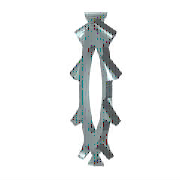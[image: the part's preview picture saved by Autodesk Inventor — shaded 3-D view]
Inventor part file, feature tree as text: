
AUTODESK INVENTOR PART (.ipt)
format: ipt  version: 2011 (Build 150229000, 229)  size: 162,304 bytes
history: native  units: mm (DEFAULTED — no unit token found)
features: extrude x1, pattern_circular x1, other x1, plane x1
ambient origin geometry x7: Origin, YZ Plane, XY Plane, X Axis, Y Axis, Z Axis, Center Point
bodies: Body (feature_tree)
feature tree (4):
  extrude  "Cut"  Depth=14.0mm
  pattern_circular  "Cuts"  [2 undecoded]
  other  "Work Axis1"
  plane  "Work Plane1"
note: 2 required parameter values undecoded (feature->parameter linkage not recoverable at this tier; creation-order binding heuristic only, values carry confidence <= 0.55)
